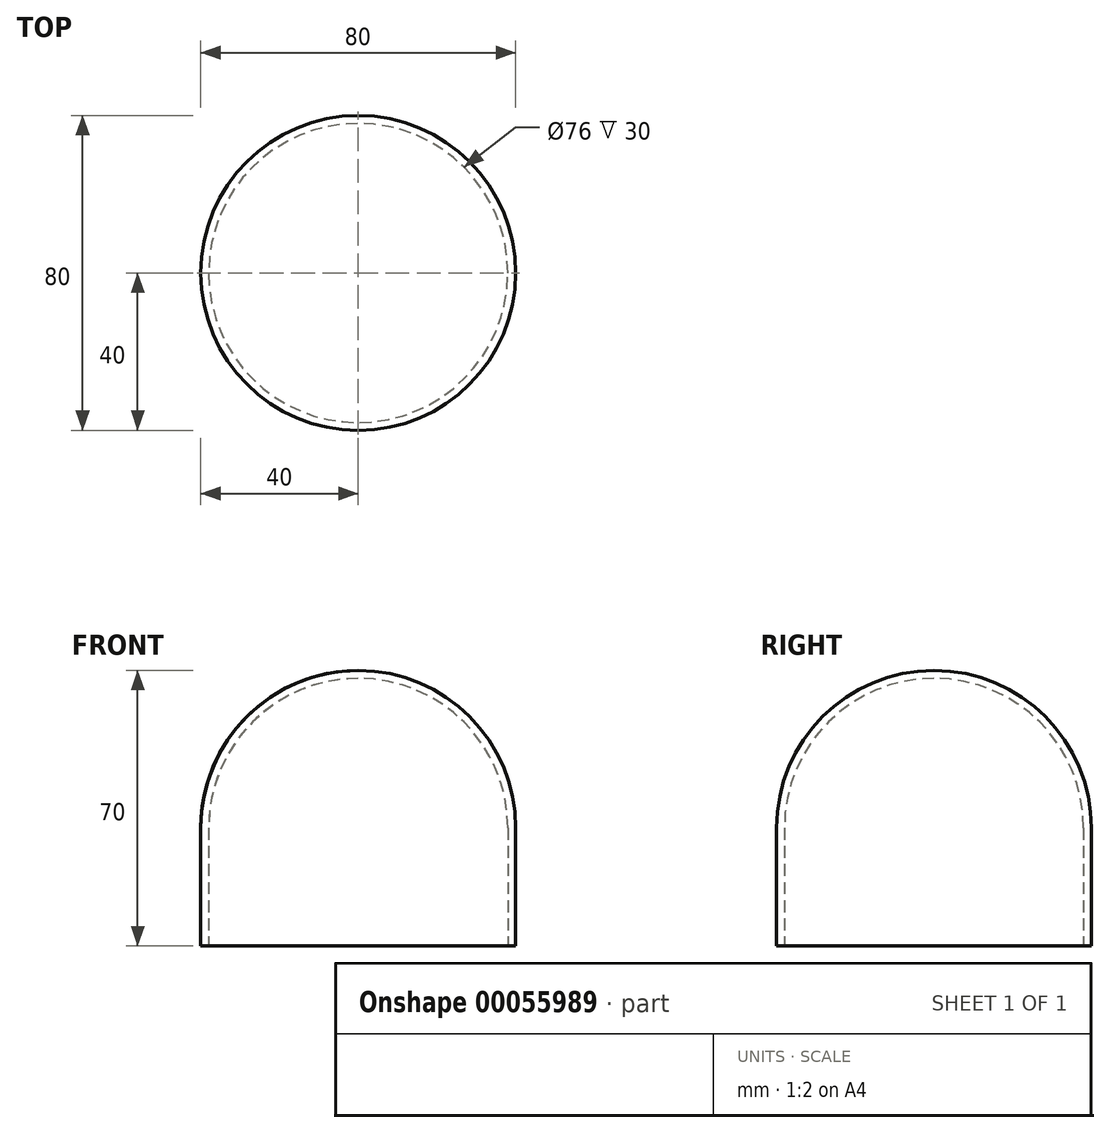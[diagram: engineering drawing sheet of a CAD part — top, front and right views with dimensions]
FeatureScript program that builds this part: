
annotation { "Feature Type Name" : "Feature", "Feature Type Description" : "" }
export const myFeature = defineFeature(function(context is Context, id is Id, definition is map)
    precondition{}
    {
        {
            var Q0;
            Q0=qCreatedBy(makeId("Front.planeOp"),FACE);
            var sketch = newSketch(context, id + "F0", { "sketchPlane" : qUnion([Q0])});
            skLineSegment(sketch, "E0", {"start": v(0, 0) * mm, "end": v(0, 30) * mm});
            skArc(sketch, "E1", {"start": v(80, 30) * mm, "mid": v(40, 70) * mm, "end": v(0, 30) * mm});
            skLineSegment(sketch, "E2", {"start": v(80, 30) * mm, "end": v(80, 0) * mm});
            skLineSegment(sketch, "E3", {"start": v(80, 0) * mm, "end": v(0, 0) * mm});
            skLineSegment(sketch, "E4", {"start": v(40, 0) * mm, "end": v(40, 87.52) * mm});
            skPoint(sketch, "E4.endSnap0", {"position": v(40, 0) * mm});
            skSolve(sketch);
        }
        {
            var Q0;
            {var subQ0=sQuery(id+"F0.wireOp",EDGE,"E0");Q0=makeQuery(id+"F0.imprint","IMPRINT",FACE,{"disambiguationData":[TD([[makeQuery(id+"F0.imprint","IMPRINT",EDGE,{"derivedFrom":subQ0}),-1.0]])]});}
            var Q1;
            Q1=sQuery(id+"F0.wireOp",EDGE,"E4");
            revolve(context, id + "F1", {"entities" : qUnion([Q0]), "axis" : qUnion([Q1]), "revolveType" : RevolveType.FULL});
        }
        {
            var Q0;
            Q0=makeQuery(id+"F1.opRevolve","SWEPT_FACE",FACE,{"disambiguationData":[OSD([sQuery(id+"F0.wireOp",EDGE,"E3")])]});
            shell(context, id + "F2", {"entities" : qUnion([Q0]), "thickness" : 2 * mm});
        }
    });
